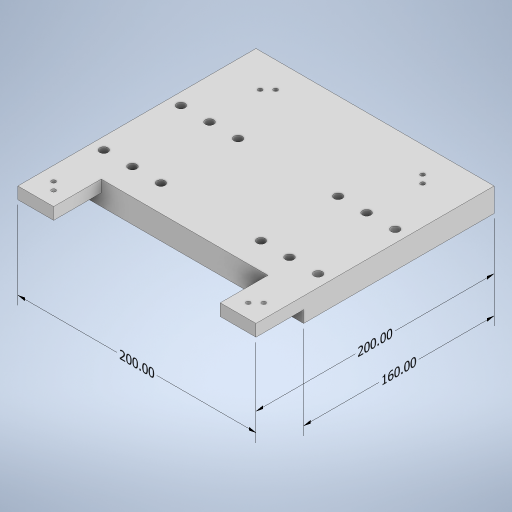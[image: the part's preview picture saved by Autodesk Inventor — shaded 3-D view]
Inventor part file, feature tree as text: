
AUTODESK INVENTOR PART (.ipt)
format: ipt  version: 2023 (Build 270158000, 158)  size: 321,024 bytes
history: native  units: mm
features: other x5, sketch x5, extrude x4, hole x1
ambient origin geometry x8: Origin, YZ Plane, XZ Plane, XY Plane, X Axis, Y Axis, Z Axis, Center Point
bodies: Body1 (feature_tree)
feature tree (15):
  other  "Sólido1"
  other  "Anotaciones"
  extrude  "Extrusión1"  Depth=160.0mm
  extrude  "Extrusión2"  TaperAngle=0.0deg  [1 undecoded]
  extrude  "Extrusión3"  Depth=20.0mm TaperAngle=0.0deg
  extrude  "Extrusión4"  Depth=10.0mm
  hole  "Agujero1"  [1 undecoded]
  sketch  "Boceto1"  dims[d0=200.0mm d1=160.0mm]
  sketch  "Boceto2"  dims[d2=20.0mm d3=0.0mm]
  sketch  "Boceto3"  dims[d4=7.0mm d5=68.0mm d6=80.0mm d7=7.6mm d8=10.0mm d9=7.0mm d10=24.0mm d11=10.0mm d16=0.0mm]
  sketch  "Boceto4"  dims[d19=40.0mm d20=20.0mm d21=0.0mm]
  sketch  "Boceto5"  dims[d22=30.0mm d23=10.0mm d24=40.0mm d25=0.0mm d26=1.75mm d27=8.25mm d28=20.0mm d29=10.0mm d30=10.0mm d31=1.75mm d32=1.75mm d33=1.75mm d34=40.0mm d35=0.0mm d36=11.749873mm d37=40.0mm d38=29.999873mm d39=21.75mm d40=11.75mm d41=28.300341mm d42=11.749873mm d43=0.0mm d44=0.0mm d45=3.5mm d46=6.0mm d47=4.0mm d48=2.0mm d49=90.0deg d50=8.0mm d51=20.594885mm d58=30.0mm d59=30.0mm d52=6.692993mm d53=5.009025mm d54=200.0mm d55=6.065637mm d56=3.288093mm d57=200.0mm d60=3.204885mm d61=4.144173mm d62=160.0mm]
  other  "Cota lineal 1"
  other  "Cota lineal 2"
  other  "Cota lineal 3"
note: 2 required parameter values undecoded (feature->parameter linkage not recoverable at this tier; creation-order binding heuristic only, values carry confidence <= 0.55)
